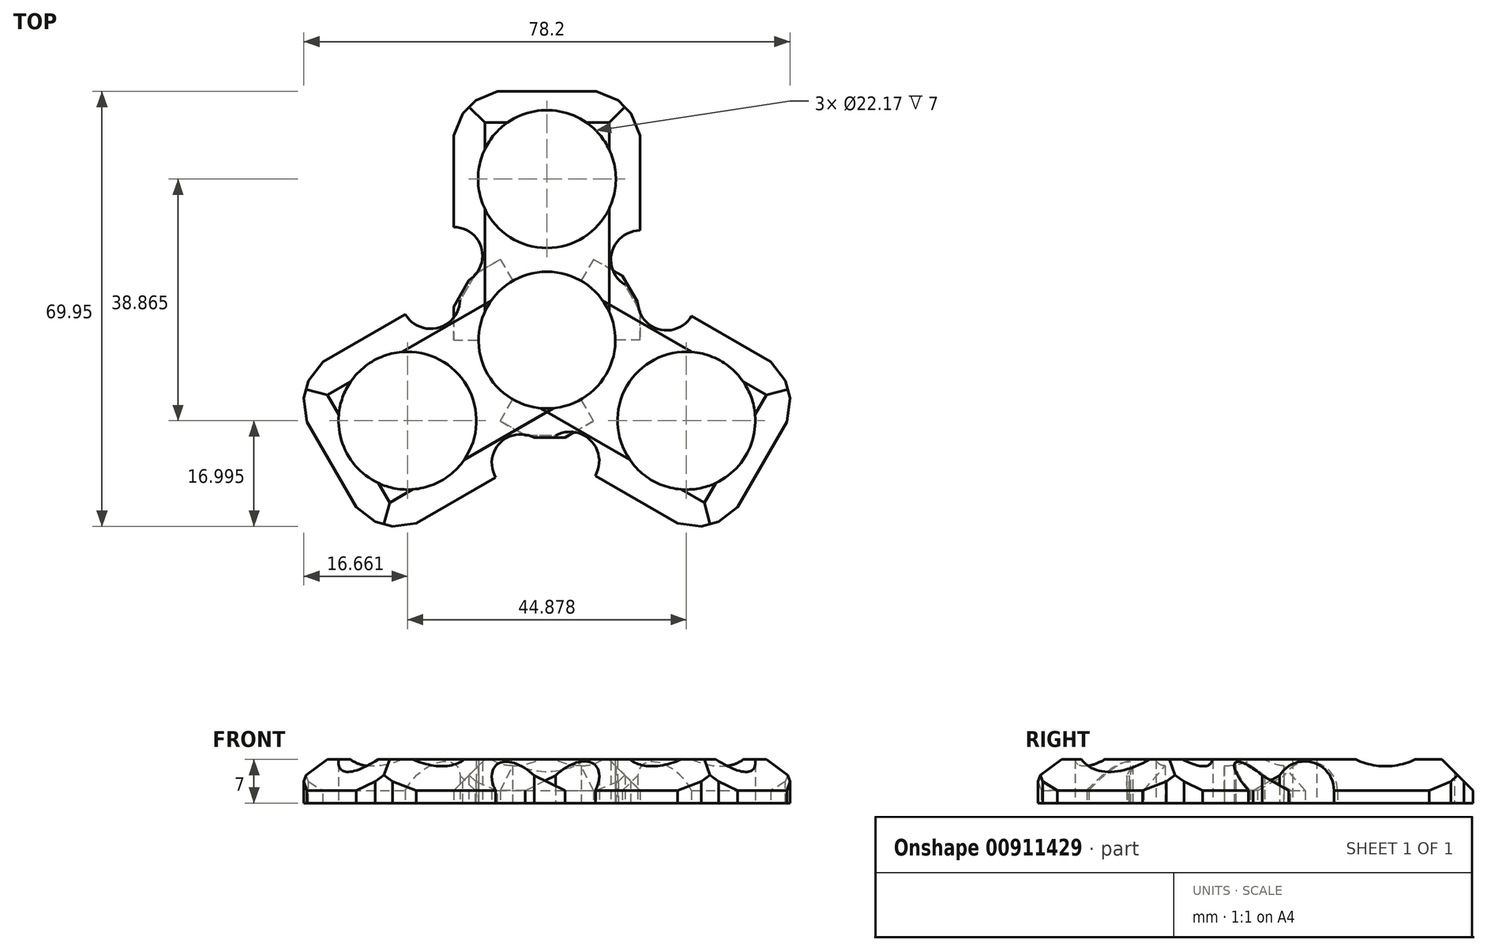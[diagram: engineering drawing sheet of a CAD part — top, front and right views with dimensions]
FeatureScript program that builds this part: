
annotation { "Feature Type Name" : "Feature", "Feature Type Description" : "" }
export const myFeature = defineFeature(function(context is Context, id is Id, definition is map)
    precondition{}
    {
        {
            var Q0;
            Q0=qCreatedBy(makeId("Top.planeOp"),FACE);
            var sketch = newSketch(context, id + "F0", { "sketchPlane" : qUnion([Q0])});
            skCircle(sketch, "E0", {"center": v(0, 0) * mm, "radius": 11 * mm});
            skLineSegment(sketch, "E1.bottom", {"start": v(0, 0) * mm, "end": v(15, 0) * mm});
            skLineSegment(sketch, "E1.top", {"start": v(0, 40) * mm, "end": v(15, 40) * mm});
            skLineSegment(sketch, "E1.left", {"start": v(0, 0) * mm, "end": v(0, 40) * mm});
            skLineSegment(sketch, "E1.right", {"start": v(15, 0) * mm, "end": v(15, 40) * mm});
            skLineSegment(sketch, "E2.bottom", {"start": v(0, 0) * mm, "end": v(-15, 0) * mm});
            skLineSegment(sketch, "E2.top", {"start": v(0, 40) * mm, "end": v(-15, 40) * mm});
            skLineSegment(sketch, "E2.right", {"start": v(-15, 0) * mm, "end": v(-15, 40) * mm});
            skLineSegment(sketch, "E3", {"start": v(0, 40) * mm, "end": v(0, 25.91) * mm});
            skCircle(sketch, "E4", {"center": v(0, 25.91) * mm, "radius": 11.08 * mm});
            skCircle(sketch, "E5", {"center": v(-15, 13.56) * mm, "radius": 4.64 * mm});
            skCircle(sketch, "E6", {"center": v(15, 12.93) * mm, "radius": 4.72 * mm});
            skSolve(sketch);
        }
        {
            var Q0;
            {var subQ0=sQuery(id+"F0.wireOp",EDGE,"E2.top");Q0=makeQuery(id+"F0.imprint","IMPRINT",FACE,{"disambiguationData":[TD([[makeQuery(id+"F0.imprint","IMPRINT",EDGE,{"derivedFrom":subQ0}),1.0]])]});}
            var Q1;
            {var subQ9=sQuery(id+"F0.wireOp",EDGE,"E1.top");Q1=makeQuery(id+"F0.imprint","IMPRINT",FACE,{"disambiguationData":[TD([[makeQuery(id+"F0.imprint","IMPRINT",EDGE,{"derivedFrom":subQ9}),-1.0]])]});}
            extrude(context, id + "F1", {"entities" : qUnion([Q0, Q1]), "depth" : 7 * mm, "offsetDistance" : 25 * mm});
        }
        {
            var Q0;
            Q0=qCreatedBy(makeId("Right.planeOp"),FACE);
            var sketch = newSketch(context, id + "F2", { "sketchPlane" : qUnion([Q0])});
            skLineSegment(sketch, "E7", {"start": v(0, 0) * mm, "end": v(0, 30.06) * mm});
            skSolve(sketch);
        }
        {
            var Q0;
            Q0=makeQuery(id+"F1.opExtrude","SWEPT_BODY",BODY,{"disambiguationData":[OSD([sQuery(id+"F0.wireOp",EDGE,"E0"),sQuery(id+"F0.wireOp",EDGE,"E1.bottom"),sQuery(id+"F0.wireOp",EDGE,"E1.top"),sQuery(id+"F0.wireOp",EDGE,"E1.right"),sQuery(id+"F0.wireOp",EDGE,"E2.bottom"),sQuery(id+"F0.wireOp",EDGE,"E2.top"),sQuery(id+"F0.wireOp",EDGE,"E2.right"),sQuery(id+"F0.wireOp",EDGE,"E4")])]});
            var Q1;
            Q1=sQuery(id+"F2.wireOp",EDGE,"E7");
            transform(context, id + "F3", {"entities" : qUnion([Q0]), "transformType" : TransformType.ROTATION, "transformAxis" : qUnion([Q1]), "angle" : 120 * degree, "makeCopy" : true});
        }
        {
            var Q0;
            Q0=qCreatedBy(makeId("Front.planeOp"),FACE);
            var sketch = newSketch(context, id + "F4", { "sketchPlane" : qUnion([Q0])});
            skLineSegment(sketch, "E8", {"start": v(0, 0) * mm, "end": v(0, 12.2) * mm});
            skSolve(sketch);
        }
        {
            var Q0;
            Q0=makeQuery(id+"F1.opExtrude","SWEPT_BODY",BODY,{"disambiguationData":[OSD([sQuery(id+"F0.wireOp",EDGE,"E0"),sQuery(id+"F0.wireOp",EDGE,"E1.bottom"),sQuery(id+"F0.wireOp",EDGE,"E1.top"),sQuery(id+"F0.wireOp",EDGE,"E1.right"),sQuery(id+"F0.wireOp",EDGE,"E2.bottom"),sQuery(id+"F0.wireOp",EDGE,"E2.top"),sQuery(id+"F0.wireOp",EDGE,"E2.right"),sQuery(id+"F0.wireOp",EDGE,"E4")])]});
            var Q1;
            Q1=sQuery(id+"F4.wireOp",EDGE,"E8");
            transform(context, id + "F5", {"entities" : qUnion([Q0]), "transformType" : TransformType.ROTATION, "transformAxis" : qUnion([Q1]), "angle" : 240 * degree, "makeCopy" : true});
        }
        {
            var Q0;
            Q0=makeQuery(id+"F1.opExtrude","SWEPT_EDGE",EDGE,{"disambiguationData":[OSD([sQuery(id+"F0.wireOp",EDGE,"E2.top"),sQuery(id+"F0.wireOp",EDGE,"E2.right")])]});
            var Q1;
            Q1=makeQuery(id+"F1.opExtrude","SWEPT_EDGE",EDGE,{"disambiguationData":[OSD([sQuery(id+"F0.wireOp",EDGE,"E1.top"),sQuery(id+"F0.wireOp",EDGE,"E1.right")])]});
            var Q2;
            Q2=makeQuery(id+"F3.opPattern","COPY",EDGE,{"derivedFrom":makeQuery(id+"F1.opExtrude","SWEPT_EDGE",EDGE,{"disambiguationData":[OSD([sQuery(id+"F0.wireOp",EDGE,"E1.top"),sQuery(id+"F0.wireOp",EDGE,"E1.right")])]}),"instanceName":"1"});
            var Q3;
            Q3=makeQuery(id+"F3.opPattern","COPY",EDGE,{"derivedFrom":makeQuery(id+"F1.opExtrude","SWEPT_EDGE",EDGE,{"disambiguationData":[OSD([sQuery(id+"F0.wireOp",EDGE,"E2.top"),sQuery(id+"F0.wireOp",EDGE,"E2.right")])]}),"instanceName":"1"});
            var Q4;
            Q4=makeQuery(id+"F5.opPattern","COPY",EDGE,{"derivedFrom":makeQuery(id+"F1.opExtrude","SWEPT_EDGE",EDGE,{"disambiguationData":[OSD([sQuery(id+"F0.wireOp",EDGE,"E1.top"),sQuery(id+"F0.wireOp",EDGE,"E1.right")])]}),"instanceName":"1"});
            var Q5;
            Q5=makeQuery(id+"F5.opPattern","COPY",EDGE,{"derivedFrom":makeQuery(id+"F1.opExtrude","SWEPT_EDGE",EDGE,{"disambiguationData":[OSD([sQuery(id+"F0.wireOp",EDGE,"E2.top"),sQuery(id+"F0.wireOp",EDGE,"E2.right")])]}),"instanceName":"1"});
            chamfer(context, id + "F6", {"entities" : qUnion([Q0, Q1, Q2, Q3, Q4, Q5]), "width" : 5 * mm, "tangentPropagation" : true});
        }
        {
            var Q0;
            {var subQ0=sQuery(id+"F0.wireOp",EDGE,"E6");var subQ1=sQuery(id+"F0.wireOp",EDGE,"E1.right");Q0=makeQuery(id+"F1.opExtrude","SWEPT_EDGE",EDGE,{"disambiguationData":[OSD([subQ1,subQ0]),TDD([makeQuery(id+"F0.imprint","INTERSECT",VERTEX,{"disambiguationData":[OD(1.0)],"derivedFrom":[subQ1,subQ0]})])]});}
            var Q1;
            {var subQ0=sQuery(id+"F0.wireOp",EDGE,"E5");var subQ1=sQuery(id+"F0.wireOp",EDGE,"E2.right");Q1=makeQuery(id+"F5.opPattern","COPY",EDGE,{"derivedFrom":makeQuery(id+"F1.opExtrude","SWEPT_EDGE",EDGE,{"disambiguationData":[OSD([subQ1,subQ0]),TDD([makeQuery(id+"F0.imprint","INTERSECT",VERTEX,{"disambiguationData":[OD(1.0)],"derivedFrom":[subQ1,subQ0]})])]}),"instanceName":"1"});}
            var Q2;
            {var subQ0=sQuery(id+"F0.wireOp",EDGE,"E6");var subQ1=sQuery(id+"F0.wireOp",EDGE,"E1.right");Q2=makeQuery(id+"F5.opPattern","COPY",EDGE,{"derivedFrom":makeQuery(id+"F1.opExtrude","SWEPT_EDGE",EDGE,{"disambiguationData":[OSD([subQ1,subQ0]),TDD([makeQuery(id+"F0.imprint","INTERSECT",VERTEX,{"disambiguationData":[OD(1.0)],"derivedFrom":[subQ1,subQ0]})])]}),"instanceName":"1"});}
            var Q3;
            {var subQ0=sQuery(id+"F0.wireOp",EDGE,"E5");var subQ1=sQuery(id+"F0.wireOp",EDGE,"E2.right");Q3=makeQuery(id+"F3.opPattern","COPY",EDGE,{"derivedFrom":makeQuery(id+"F1.opExtrude","SWEPT_EDGE",EDGE,{"disambiguationData":[OSD([subQ1,subQ0]),TDD([makeQuery(id+"F0.imprint","INTERSECT",VERTEX,{"disambiguationData":[OD(1.0)],"derivedFrom":[subQ1,subQ0]})])]}),"instanceName":"1"});}
            var Q4;
            {var subQ0=sQuery(id+"F0.wireOp",EDGE,"E6");var subQ1=sQuery(id+"F0.wireOp",EDGE,"E1.right");Q4=makeQuery(id+"F3.opPattern","COPY",EDGE,{"derivedFrom":makeQuery(id+"F1.opExtrude","SWEPT_EDGE",EDGE,{"disambiguationData":[OSD([subQ1,subQ0]),TDD([makeQuery(id+"F0.imprint","INTERSECT",VERTEX,{"disambiguationData":[OD(1.0)],"derivedFrom":[subQ1,subQ0]})])]}),"instanceName":"1"});}
            var Q5;
            {var subQ0=sQuery(id+"F0.wireOp",EDGE,"E5");var subQ1=sQuery(id+"F0.wireOp",EDGE,"E2.right");Q5=makeQuery(id+"F1.opExtrude","SWEPT_EDGE",EDGE,{"disambiguationData":[OSD([subQ1,subQ0]),TDD([makeQuery(id+"F0.imprint","INTERSECT",VERTEX,{"disambiguationData":[OD(1.0)],"derivedFrom":[subQ1,subQ0]})])]});}
            chamfer(context, id + "F7", {"entities" : qUnion([Q0, Q1, Q2, Q3, Q4, Q5]), "width" : 5 * mm, "tangentPropagation" : true});
        }
        {
            var Q0;
            {var subQ0=sQuery(id+"F0.wireOp",EDGE,"E2.right");Q0=makeQuery(id+"F3.opPattern","COPY",EDGE,{"derivedFrom":makeQuery(id+"F1.opExtrude","CAP_EDGE",EDGE,{"disambiguationData":[OSD([subQ0]),TDD([makeQuery(id+"F0.imprint","IMPRINT",EDGE,{"disambiguationData":[TD([[makeQuery(id+"F0.imprint","INTERSECT",VERTEX,{"derivedFrom":[sQuery(id+"F0.wireOp",EDGE,"E2.top"),subQ0]}),1.0]])],"derivedFrom":subQ0})])],"isStart":false}),"instanceName":"1"});}
            var Q1;
            {var subQ0=sQuery(id+"F0.wireOp",EDGE,"E1.right");Q1=makeQuery(id+"F3.opPattern","COPY",EDGE,{"derivedFrom":makeQuery(id+"F1.opExtrude","CAP_EDGE",EDGE,{"disambiguationData":[OSD([subQ0]),TDD([makeQuery(id+"F0.imprint","IMPRINT",EDGE,{"disambiguationData":[TD([[makeQuery(id+"F0.imprint","INTERSECT",VERTEX,{"derivedFrom":[sQuery(id+"F0.wireOp",EDGE,"E1.top"),subQ0]}),1.0]])],"derivedFrom":subQ0})])],"isStart":false}),"instanceName":"1"});}
            var Q2;
            {var subQ0=sQuery(id+"F0.wireOp",EDGE,"E2.right");Q2=makeQuery(id+"F1.opExtrude","CAP_EDGE",EDGE,{"disambiguationData":[OSD([subQ0]),TDD([makeQuery(id+"F0.imprint","IMPRINT",EDGE,{"disambiguationData":[TD([[makeQuery(id+"F0.imprint","INTERSECT",VERTEX,{"derivedFrom":[sQuery(id+"F0.wireOp",EDGE,"E2.top"),subQ0]}),1.0]])],"derivedFrom":subQ0})])],"isStart":false});}
            var Q3;
            {var subQ0=sQuery(id+"F0.wireOp",EDGE,"E1.right");Q3=makeQuery(id+"F1.opExtrude","CAP_EDGE",EDGE,{"disambiguationData":[OSD([subQ0]),TDD([makeQuery(id+"F0.imprint","IMPRINT",EDGE,{"disambiguationData":[TD([[makeQuery(id+"F0.imprint","INTERSECT",VERTEX,{"derivedFrom":[sQuery(id+"F0.wireOp",EDGE,"E1.top"),subQ0]}),1.0]])],"derivedFrom":subQ0})])],"isStart":false});}
            var Q4;
            {var subQ0=sQuery(id+"F0.wireOp",EDGE,"E2.right");Q4=makeQuery(id+"F5.opPattern","COPY",EDGE,{"derivedFrom":makeQuery(id+"F1.opExtrude","CAP_EDGE",EDGE,{"disambiguationData":[OSD([subQ0]),TDD([makeQuery(id+"F0.imprint","IMPRINT",EDGE,{"disambiguationData":[TD([[makeQuery(id+"F0.imprint","INTERSECT",VERTEX,{"derivedFrom":[sQuery(id+"F0.wireOp",EDGE,"E2.top"),subQ0]}),1.0]])],"derivedFrom":subQ0})])],"isStart":false}),"instanceName":"1"});}
            var Q5;
            {var subQ0=sQuery(id+"F0.wireOp",EDGE,"E1.right");Q5=makeQuery(id+"F5.opPattern","COPY",EDGE,{"derivedFrom":makeQuery(id+"F1.opExtrude","CAP_EDGE",EDGE,{"disambiguationData":[OSD([subQ0]),TDD([makeQuery(id+"F0.imprint","IMPRINT",EDGE,{"disambiguationData":[TD([[makeQuery(id+"F0.imprint","INTERSECT",VERTEX,{"derivedFrom":[sQuery(id+"F0.wireOp",EDGE,"E1.top"),subQ0]}),1.0]])],"derivedFrom":subQ0})])],"isStart":false}),"instanceName":"1"});}
            var Q6;
            Q6=makeQuery(id+"F5.opPattern","COPY",EDGE,{"derivedFrom":makeQuery(id+"F1.opExtrude","CAP_EDGE",EDGE,{"disambiguationData":[OSD([sQuery(id+"F0.wireOp",EDGE,"E1.top"),sQuery(id+"F0.wireOp",EDGE,"E2.top")])],"isStart":false}),"instanceName":"1"});
            var Q7;
            Q7=makeQuery(id+"F3.opPattern","COPY",EDGE,{"derivedFrom":makeQuery(id+"F1.opExtrude","CAP_EDGE",EDGE,{"disambiguationData":[OSD([sQuery(id+"F0.wireOp",EDGE,"E1.top"),sQuery(id+"F0.wireOp",EDGE,"E2.top")])],"isStart":false}),"instanceName":"1"});
            chamfer(context, id + "F8", {"entities" : qUnion([Q0, Q1, Q2, Q3, Q4, Q5, Q6, Q7]), "width" : 5 * mm, "tangentPropagation" : true});
        }
        {
            var Q0;
            {var subQ0=sQuery(id+"F0.wireOp",EDGE,"E1.top");Q0=makeQuery(id+"F6.opChamfer","BLEND_EDGE",EDGE,{"blendedFrom":[makeQuery(id+"F1.opExtrude","SWEPT_EDGE",EDGE,{"disambiguationData":[OSD([subQ0,sQuery(id+"F0.wireOp",EDGE,"E1.right")])]}),makeQuery(id+"F1.opExtrude","SWEPT_FACE",FACE,{"disambiguationData":[OSD([subQ0,sQuery(id+"F0.wireOp",EDGE,"E2.top")])]})],"blendedInto":[makeQuery(id+"F1.opExtrude","SWEPT_FACE",FACE,{"disambiguationData":[OSD([subQ0,sQuery(id+"F0.wireOp",EDGE,"E2.top")])]})]});}
            var Q1;
            {var subQ0=sQuery(id+"F0.wireOp",EDGE,"E1.right");var subQ1=sQuery(id+"F0.wireOp",EDGE,"E1.top");Q1=makeQuery(id+"F6.opChamfer","BLEND_EDGE",EDGE,{"blendedFrom":[makeQuery(id+"F1.opExtrude","SWEPT_EDGE",EDGE,{"disambiguationData":[OSD([subQ1,subQ0])]}),makeQuery(id+"F1.opExtrude","SWEPT_FACE",FACE,{"disambiguationData":[OSD([subQ0]),TDD([makeQuery(id+"F0.imprint","IMPRINT",EDGE,{"disambiguationData":[TD([[makeQuery(id+"F0.imprint","INTERSECT",VERTEX,{"derivedFrom":[subQ1,subQ0]}),1.0]])],"derivedFrom":subQ0})])]})],"blendedInto":[makeQuery(id+"F1.opExtrude","SWEPT_FACE",FACE,{"disambiguationData":[OSD([subQ0]),TDD([makeQuery(id+"F0.imprint","IMPRINT",EDGE,{"disambiguationData":[TD([[makeQuery(id+"F0.imprint","INTERSECT",VERTEX,{"derivedFrom":[subQ1,subQ0]}),1.0]])],"derivedFrom":subQ0})])]})]});}
            var Q2;
            {var subQ0=sQuery(id+"F0.wireOp",EDGE,"E2.top");Q2=makeQuery(id+"F6.opChamfer","BLEND_EDGE",EDGE,{"blendedFrom":[makeQuery(id+"F1.opExtrude","SWEPT_EDGE",EDGE,{"disambiguationData":[OSD([subQ0,sQuery(id+"F0.wireOp",EDGE,"E2.right")])]}),makeQuery(id+"F1.opExtrude","SWEPT_FACE",FACE,{"disambiguationData":[OSD([sQuery(id+"F0.wireOp",EDGE,"E1.top"),subQ0])]})],"blendedInto":[makeQuery(id+"F1.opExtrude","SWEPT_FACE",FACE,{"disambiguationData":[OSD([sQuery(id+"F0.wireOp",EDGE,"E1.top"),subQ0])]})]});}
            var Q3;
            {var subQ0=sQuery(id+"F0.wireOp",EDGE,"E2.right");var subQ1=sQuery(id+"F0.wireOp",EDGE,"E2.top");Q3=makeQuery(id+"F6.opChamfer","BLEND_EDGE",EDGE,{"blendedFrom":[makeQuery(id+"F1.opExtrude","SWEPT_EDGE",EDGE,{"disambiguationData":[OSD([subQ1,subQ0])]}),makeQuery(id+"F1.opExtrude","SWEPT_FACE",FACE,{"disambiguationData":[OSD([subQ0]),TDD([makeQuery(id+"F0.imprint","IMPRINT",EDGE,{"disambiguationData":[TD([[makeQuery(id+"F0.imprint","INTERSECT",VERTEX,{"derivedFrom":[subQ1,subQ0]}),1.0]])],"derivedFrom":subQ0})])]})],"blendedInto":[makeQuery(id+"F1.opExtrude","SWEPT_FACE",FACE,{"disambiguationData":[OSD([subQ0]),TDD([makeQuery(id+"F0.imprint","IMPRINT",EDGE,{"disambiguationData":[TD([[makeQuery(id+"F0.imprint","INTERSECT",VERTEX,{"derivedFrom":[subQ1,subQ0]}),1.0]])],"derivedFrom":subQ0})])]})]});}
            var Q4;
            {var subQ0=sQuery(id+"F0.wireOp",EDGE,"E2.top");Q4=makeQuery(id+"F6.opChamfer","BLEND_EDGE",EDGE,{"blendedFrom":[makeQuery(id+"F5.opPattern","COPY",EDGE,{"derivedFrom":makeQuery(id+"F1.opExtrude","SWEPT_EDGE",EDGE,{"disambiguationData":[OSD([subQ0,sQuery(id+"F0.wireOp",EDGE,"E2.right")])]}),"instanceName":"1"}),makeQuery(id+"F5.opPattern","COPY",FACE,{"derivedFrom":makeQuery(id+"F1.opExtrude","SWEPT_FACE",FACE,{"disambiguationData":[OSD([sQuery(id+"F0.wireOp",EDGE,"E1.top"),subQ0])]}),"instanceName":"1"})],"blendedInto":[makeQuery(id+"F5.opPattern","COPY",FACE,{"derivedFrom":makeQuery(id+"F1.opExtrude","SWEPT_FACE",FACE,{"disambiguationData":[OSD([sQuery(id+"F0.wireOp",EDGE,"E1.top"),subQ0])]}),"instanceName":"1"})]});}
            var Q5;
            {var subQ0=sQuery(id+"F0.wireOp",EDGE,"E2.right");var subQ1=sQuery(id+"F0.wireOp",EDGE,"E2.top");Q5=makeQuery(id+"F6.opChamfer","BLEND_EDGE",EDGE,{"blendedFrom":[makeQuery(id+"F5.opPattern","COPY",EDGE,{"derivedFrom":makeQuery(id+"F1.opExtrude","SWEPT_EDGE",EDGE,{"disambiguationData":[OSD([subQ1,subQ0])]}),"instanceName":"1"}),makeQuery(id+"F5.opPattern","COPY",FACE,{"derivedFrom":makeQuery(id+"F1.opExtrude","SWEPT_FACE",FACE,{"disambiguationData":[OSD([subQ0]),TDD([makeQuery(id+"F0.imprint","IMPRINT",EDGE,{"disambiguationData":[TD([[makeQuery(id+"F0.imprint","INTERSECT",VERTEX,{"derivedFrom":[subQ1,subQ0]}),1.0]])],"derivedFrom":subQ0})])]}),"instanceName":"1"})],"blendedInto":[makeQuery(id+"F5.opPattern","COPY",FACE,{"derivedFrom":makeQuery(id+"F1.opExtrude","SWEPT_FACE",FACE,{"disambiguationData":[OSD([subQ0]),TDD([makeQuery(id+"F0.imprint","IMPRINT",EDGE,{"disambiguationData":[TD([[makeQuery(id+"F0.imprint","INTERSECT",VERTEX,{"derivedFrom":[subQ1,subQ0]}),1.0]])],"derivedFrom":subQ0})])]}),"instanceName":"1"})]});}
            var Q6;
            {var subQ0=sQuery(id+"F0.wireOp",EDGE,"E1.right");var subQ1=sQuery(id+"F0.wireOp",EDGE,"E1.top");Q6=makeQuery(id+"F6.opChamfer","BLEND_EDGE",EDGE,{"blendedFrom":[makeQuery(id+"F5.opPattern","COPY",EDGE,{"derivedFrom":makeQuery(id+"F1.opExtrude","SWEPT_EDGE",EDGE,{"disambiguationData":[OSD([subQ1,subQ0])]}),"instanceName":"1"}),makeQuery(id+"F5.opPattern","COPY",FACE,{"derivedFrom":makeQuery(id+"F1.opExtrude","SWEPT_FACE",FACE,{"disambiguationData":[OSD([subQ0]),TDD([makeQuery(id+"F0.imprint","IMPRINT",EDGE,{"disambiguationData":[TD([[makeQuery(id+"F0.imprint","INTERSECT",VERTEX,{"derivedFrom":[subQ1,subQ0]}),1.0]])],"derivedFrom":subQ0})])]}),"instanceName":"1"})],"blendedInto":[makeQuery(id+"F5.opPattern","COPY",FACE,{"derivedFrom":makeQuery(id+"F1.opExtrude","SWEPT_FACE",FACE,{"disambiguationData":[OSD([subQ0]),TDD([makeQuery(id+"F0.imprint","IMPRINT",EDGE,{"disambiguationData":[TD([[makeQuery(id+"F0.imprint","INTERSECT",VERTEX,{"derivedFrom":[subQ1,subQ0]}),1.0]])],"derivedFrom":subQ0})])]}),"instanceName":"1"})]});}
            var Q7;
            {var subQ0=sQuery(id+"F0.wireOp",EDGE,"E1.top");Q7=makeQuery(id+"F6.opChamfer","BLEND_EDGE",EDGE,{"blendedFrom":[makeQuery(id+"F5.opPattern","COPY",EDGE,{"derivedFrom":makeQuery(id+"F1.opExtrude","SWEPT_EDGE",EDGE,{"disambiguationData":[OSD([subQ0,sQuery(id+"F0.wireOp",EDGE,"E1.right")])]}),"instanceName":"1"}),makeQuery(id+"F5.opPattern","COPY",FACE,{"derivedFrom":makeQuery(id+"F1.opExtrude","SWEPT_FACE",FACE,{"disambiguationData":[OSD([subQ0,sQuery(id+"F0.wireOp",EDGE,"E2.top")])]}),"instanceName":"1"})],"blendedInto":[makeQuery(id+"F5.opPattern","COPY",FACE,{"derivedFrom":makeQuery(id+"F1.opExtrude","SWEPT_FACE",FACE,{"disambiguationData":[OSD([subQ0,sQuery(id+"F0.wireOp",EDGE,"E2.top")])]}),"instanceName":"1"})]});}
            var Q8;
            {var subQ0=sQuery(id+"F0.wireOp",EDGE,"E2.top");Q8=makeQuery(id+"F6.opChamfer","BLEND_EDGE",EDGE,{"blendedFrom":[makeQuery(id+"F3.opPattern","COPY",EDGE,{"derivedFrom":makeQuery(id+"F1.opExtrude","SWEPT_EDGE",EDGE,{"disambiguationData":[OSD([subQ0,sQuery(id+"F0.wireOp",EDGE,"E2.right")])]}),"instanceName":"1"}),makeQuery(id+"F3.opPattern","COPY",FACE,{"derivedFrom":makeQuery(id+"F1.opExtrude","SWEPT_FACE",FACE,{"disambiguationData":[OSD([sQuery(id+"F0.wireOp",EDGE,"E1.top"),subQ0])]}),"instanceName":"1"})],"blendedInto":[makeQuery(id+"F3.opPattern","COPY",FACE,{"derivedFrom":makeQuery(id+"F1.opExtrude","SWEPT_FACE",FACE,{"disambiguationData":[OSD([sQuery(id+"F0.wireOp",EDGE,"E1.top"),subQ0])]}),"instanceName":"1"})]});}
            var Q9;
            {var subQ0=sQuery(id+"F0.wireOp",EDGE,"E2.right");var subQ1=sQuery(id+"F0.wireOp",EDGE,"E2.top");Q9=makeQuery(id+"F6.opChamfer","BLEND_EDGE",EDGE,{"blendedFrom":[makeQuery(id+"F3.opPattern","COPY",EDGE,{"derivedFrom":makeQuery(id+"F1.opExtrude","SWEPT_EDGE",EDGE,{"disambiguationData":[OSD([subQ1,subQ0])]}),"instanceName":"1"}),makeQuery(id+"F3.opPattern","COPY",FACE,{"derivedFrom":makeQuery(id+"F1.opExtrude","SWEPT_FACE",FACE,{"disambiguationData":[OSD([subQ0]),TDD([makeQuery(id+"F0.imprint","IMPRINT",EDGE,{"disambiguationData":[TD([[makeQuery(id+"F0.imprint","INTERSECT",VERTEX,{"derivedFrom":[subQ1,subQ0]}),1.0]])],"derivedFrom":subQ0})])]}),"instanceName":"1"})],"blendedInto":[makeQuery(id+"F3.opPattern","COPY",FACE,{"derivedFrom":makeQuery(id+"F1.opExtrude","SWEPT_FACE",FACE,{"disambiguationData":[OSD([subQ0]),TDD([makeQuery(id+"F0.imprint","IMPRINT",EDGE,{"disambiguationData":[TD([[makeQuery(id+"F0.imprint","INTERSECT",VERTEX,{"derivedFrom":[subQ1,subQ0]}),1.0]])],"derivedFrom":subQ0})])]}),"instanceName":"1"})]});}
            var Q10;
            {var subQ0=sQuery(id+"F0.wireOp",EDGE,"E1.right");var subQ1=sQuery(id+"F0.wireOp",EDGE,"E1.top");Q10=makeQuery(id+"F6.opChamfer","BLEND_EDGE",EDGE,{"blendedFrom":[makeQuery(id+"F3.opPattern","COPY",EDGE,{"derivedFrom":makeQuery(id+"F1.opExtrude","SWEPT_EDGE",EDGE,{"disambiguationData":[OSD([subQ1,subQ0])]}),"instanceName":"1"}),makeQuery(id+"F3.opPattern","COPY",FACE,{"derivedFrom":makeQuery(id+"F1.opExtrude","SWEPT_FACE",FACE,{"disambiguationData":[OSD([subQ0]),TDD([makeQuery(id+"F0.imprint","IMPRINT",EDGE,{"disambiguationData":[TD([[makeQuery(id+"F0.imprint","INTERSECT",VERTEX,{"derivedFrom":[subQ1,subQ0]}),1.0]])],"derivedFrom":subQ0})])]}),"instanceName":"1"})],"blendedInto":[makeQuery(id+"F3.opPattern","COPY",FACE,{"derivedFrom":makeQuery(id+"F1.opExtrude","SWEPT_FACE",FACE,{"disambiguationData":[OSD([subQ0]),TDD([makeQuery(id+"F0.imprint","IMPRINT",EDGE,{"disambiguationData":[TD([[makeQuery(id+"F0.imprint","INTERSECT",VERTEX,{"derivedFrom":[subQ1,subQ0]}),1.0]])],"derivedFrom":subQ0})])]}),"instanceName":"1"})]});}
            var Q11;
            {var subQ0=sQuery(id+"F0.wireOp",EDGE,"E1.top");Q11=makeQuery(id+"F6.opChamfer","BLEND_EDGE",EDGE,{"blendedFrom":[makeQuery(id+"F3.opPattern","COPY",EDGE,{"derivedFrom":makeQuery(id+"F1.opExtrude","SWEPT_EDGE",EDGE,{"disambiguationData":[OSD([subQ0,sQuery(id+"F0.wireOp",EDGE,"E1.right")])]}),"instanceName":"1"}),makeQuery(id+"F3.opPattern","COPY",FACE,{"derivedFrom":makeQuery(id+"F1.opExtrude","SWEPT_FACE",FACE,{"disambiguationData":[OSD([subQ0,sQuery(id+"F0.wireOp",EDGE,"E2.top")])]}),"instanceName":"1"})],"blendedInto":[makeQuery(id+"F3.opPattern","COPY",FACE,{"derivedFrom":makeQuery(id+"F1.opExtrude","SWEPT_FACE",FACE,{"disambiguationData":[OSD([subQ0,sQuery(id+"F0.wireOp",EDGE,"E2.top")])]}),"instanceName":"1"})]});}
            chamfer(context, id + "F9", {"entities" : qUnion([Q0, Q1, Q2, Q3, Q4, Q5, Q6, Q7, Q8, Q9, Q10, Q11]), "width" : 5 * mm, "tangentPropagation" : true});
        }
        {
            var Q0;
            Q0=makeQuery(id+"F1.opExtrude","CAP_EDGE",EDGE,{"disambiguationData":[OSD([sQuery(id+"F0.wireOp",EDGE,"E1.top"),sQuery(id+"F0.wireOp",EDGE,"E2.top")])],"isStart":false});
            chamfer(context, id + "F10", {"entities" : qUnion([Q0]), "width" : 5 * mm, "tangentPropagation" : true});
        }
    });
